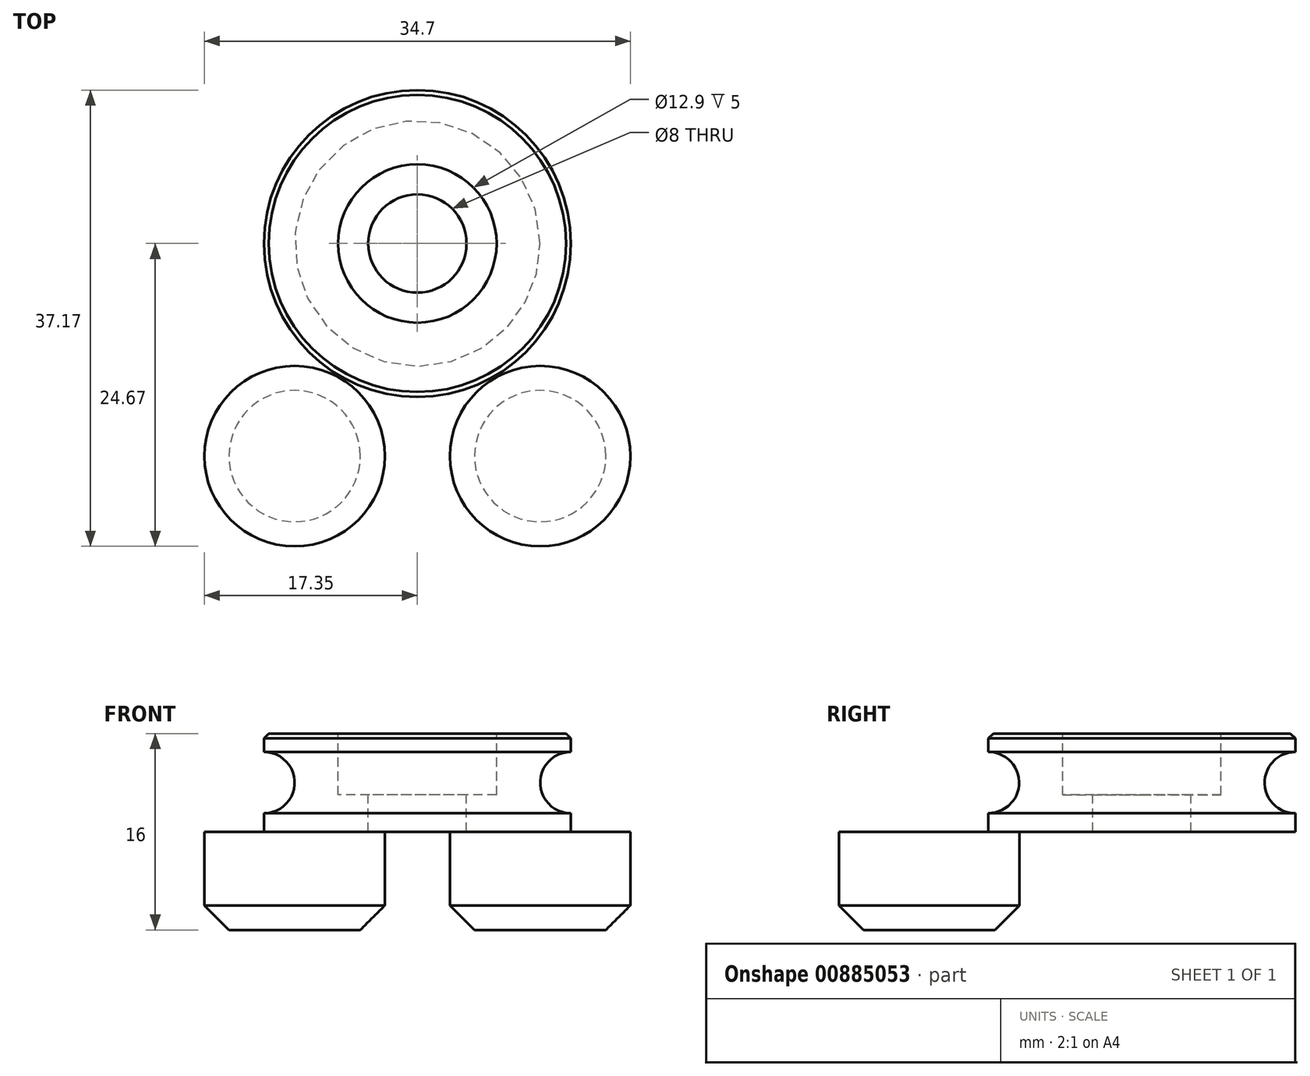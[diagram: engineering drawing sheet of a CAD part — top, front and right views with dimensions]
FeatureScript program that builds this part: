
annotation { "Feature Type Name" : "Feature", "Feature Type Description" : "" }
export const myFeature = defineFeature(function(context is Context, id is Id, definition is map)
    precondition{}
    {
        {
            var Q0;
            Q0=qCreatedBy(makeId("Top.planeOp"),FACE);
            var sketch = newSketch(context, id + "F0", { "sketchPlane" : qUnion([Q0])});
            skCircle(sketch, "E0", {"center": v(0, 0) * mm, "radius": 39 * mm});
            skCircle(sketch, "E1", {"center": v(0, 0) * mm, "radius": 2.33 * mm});
            skSolve(sketch);
        }
        {
            var Q0;
            Q0=qSketchRegion(id+"F0",true);
            extrude(context, id + "F1", {"entities" : qUnion([Q0]), "endBound" : BoundingType.SYMMETRIC, "depth" : 8 * mm, "offsetDistance" : 25 * mm});
        }
        {
            var Q0;
            Q0=qCreatedBy(makeId("Right.planeOp"),FACE);
            var sketch = newSketch(context, id + "F2", { "sketchPlane" : qUnion([Q0])});
            skLineSegment(sketch, "E2", {"start": v(43.5, 0) * mm, "end": v(-48.07, 0) * mm, "construction": true});
            skLineSegment(sketch, "E3", {"start": v(-39, -4) * mm, "end": v(-39, 4) * mm, "construction": true});
            skCircle(sketch, "E4", {"center": v(-39, 0) * mm, "radius": 2.5 * mm});
            skSolve(sketch);
        }
        {
            var Q0;
            Q0=qSketchRegion(id+"F2",true);
            var Q1;
            Q1=makeQuery(id+"F1.opExtrude","SWEPT_FACE",FACE,{"disambiguationData":[OSD([sQuery(id+"F0.wireOp",EDGE,"E1")])]});
            revolve(context, id + "F3", {"operationType" : NewBodyOperationType.REMOVE, "surfaceOperationType" : NewSurfaceOperationType.NEW, "entities" : qUnion([Q0]), "axis" : qUnion([Q1]), "revolveType" : RevolveType.FULL, "oppositeDirection" : true});
        }
        {
            var Q0;
            Q0=makeQuery(id+"F13.boolean.opBoolean","COPY",EDGE,{"derivedFrom":makeQuery(id+"F13.opExtrude","CAP_EDGE",EDGE,{"disambiguationData":[OSD([sQuery(id+"F12.wireOp",EDGE,"95e5c256-83ff-4b91-8d21-37ed4a70a4b7.2")])],"isStart":true})});
            var Q1;
            Q1=makeQuery(id+"F13.boolean.opBoolean","COPY",EDGE,{"derivedFrom":makeQuery(id+"F13.opExtrude","CAP_EDGE",EDGE,{"disambiguationData":[OSD([sQuery(id+"F12.wireOp",EDGE,"95e5c256-83ff-4b91-8d21-37ed4a70a4b7.3")])],"isStart":true})});
            var Q2;
            Q2=makeQuery(id+"F13.boolean.opBoolean","COPY",EDGE,{"derivedFrom":makeQuery(id+"F13.opExtrude","CAP_EDGE",EDGE,{"disambiguationData":[OSD([sQuery(id+"F12.wireOp",EDGE,"95e5c256-83ff-4b91-8d21-37ed4a70a4b7.4")])],"isStart":true})});
            var Q3;
            Q3=makeQuery(id+"F13.boolean.opBoolean","COPY",EDGE,{"derivedFrom":makeQuery(id+"F13.opExtrude","CAP_EDGE",EDGE,{"disambiguationData":[OSD([sQuery(id+"F12.wireOp",EDGE,"95e5c256-83ff-4b91-8d21-37ed4a70a4b7.5")])],"isStart":true})});
            var Q4;
            Q4=makeQuery(id+"F13.boolean.opBoolean","COPY",EDGE,{"derivedFrom":makeQuery(id+"F13.opExtrude","CAP_EDGE",EDGE,{"disambiguationData":[OSD([sQuery(id+"F12.wireOp",EDGE,"95e5c256-83ff-4b91-8d21-37ed4a70a4b7.0")])],"isStart":true})});
            var Q5;
            Q5=makeQuery(id+"F13.boolean.opBoolean","COPY",EDGE,{"derivedFrom":makeQuery(id+"F13.opExtrude","CAP_EDGE",EDGE,{"disambiguationData":[OSD([sQuery(id+"F12.wireOp",EDGE,"95e5c256-83ff-4b91-8d21-37ed4a70a4b7.1")])],"isStart":true})});
            var Q6;
            Q6=makeQuery(id+"F3.boolean.opBoolean","INTERSECT",EDGE,{"disambiguationData":[OD(1.0)],"derivedFrom":[makeQuery(id+"F1.opExtrude","SWEPT_FACE",FACE,{"disambiguationData":[OSD([sQuery(id+"F0.wireOp",EDGE,"E0")])]}),makeQuery(id+"F3.opRevolve","SWEPT_FACE",FACE,{"disambiguationData":[OSD([sQuery(id+"F2.wireOp",EDGE,"E4")])]})]});
            var Q7;
            Q7=makeQuery(id+"F3.boolean.opBoolean","INTERSECT",EDGE,{"disambiguationData":[OD(0.0)],"derivedFrom":[makeQuery(id+"F1.opExtrude","SWEPT_FACE",FACE,{"disambiguationData":[OSD([sQuery(id+"F0.wireOp",EDGE,"E0")])]}),makeQuery(id+"F3.opRevolve","SWEPT_FACE",FACE,{"disambiguationData":[OSD([sQuery(id+"F2.wireOp",EDGE,"E4")])]})]});
            chamfer(context, id + "F4", {"entities" : qUnion([Q0, Q1, Q2, Q3, Q4, Q5, Q6, Q7]), "width" : .5 * mm, "tangentPropagation" : true});
        }
        {
            var Q0;
            Q0=makeQuery(id+"F1.opExtrude","CAP_FACE",FACE,{"disambiguationData":[OSD([sQuery(id+"F0.wireOp",EDGE,"E0"),sQuery(id+"F0.wireOp",EDGE,"E1")])],"isStart":false});
            var sketch = newSketch(context, id + "F5", { "sketchPlane" : qUnion([Q0])});
            skCircle(sketch, "E5", {"center": v(-10, 17.32) * mm, "radius": 7.35 * mm});
            skLineSegment(sketch, "E6", {"start": v(0, -39) * mm, "end": v(0, 39) * mm, "construction": true});
            skLineSegment(sketch, "E7", {"start": v(39, 0) * mm, "end": v(-39, 0) * mm, "construction": true});
            skLineSegment(sketch, "E8", {"start": v(-2.6, -4.5) * mm, "end": v(19.5, 33.77) * mm, "construction": true});
            skLineSegment(sketch, "E9", {"start": v(2.6, -4.5) * mm, "end": v(-19.5, 33.77) * mm, "construction": true});
            skCircle(sketch, "E10", {"center": v(0, 0) * mm, "radius": 20 * mm, "construction": true});
            skCircle(sketch, "E11", {"center": v(-20, 0) * mm, "radius": 7.35 * mm});
            skCircle(sketch, "E12", {"center": v(10, 17.32) * mm, "radius": 7.35 * mm});
            skCircle(sketch, "E13", {"center": v(20, 0) * mm, "radius": 7.35 * mm});
            skCircle(sketch, "E14.MirrorC", {"center": v(10, -17.32) * mm, "radius": 7.35 * mm});
            skCircle(sketch, "E15.MirrorC", {"center": v(-10, -17.32) * mm, "radius": 7.35 * mm});
            skSolve(sketch);
        }
        {
            var Q0;
            Q0=makeQuery(id+"F5.imprint","IMPRINT",FACE,{"disambiguationData":[TD([[makeQuery(id+"F5.imprint","IMPRINT",EDGE,{"derivedFrom":sQuery(id+"F5.wireOp",EDGE,"E13")}),1.0]])]});
            var Q1;
            Q1=makeQuery(id+"F5.imprint","IMPRINT",FACE,{"disambiguationData":[TD([[makeQuery(id+"F5.imprint","IMPRINT",EDGE,{"derivedFrom":sQuery(id+"F5.wireOp",EDGE,"E14.MirrorC")}),-1.0]])]});
            var Q2;
            Q2=makeQuery(id+"F5.imprint","IMPRINT",FACE,{"disambiguationData":[TD([[makeQuery(id+"F5.imprint","IMPRINT",EDGE,{"derivedFrom":sQuery(id+"F5.wireOp",EDGE,"E15.MirrorC")}),-1.0]])]});
            var Q3;
            Q3=makeQuery(id+"F5.imprint","IMPRINT",FACE,{"disambiguationData":[TD([[makeQuery(id+"F5.imprint","IMPRINT",EDGE,{"derivedFrom":sQuery(id+"F5.wireOp",EDGE,"E11")}),1.0]])]});
            var Q4;
            Q4=makeQuery(id+"F5.imprint","IMPRINT",FACE,{"disambiguationData":[TD([[makeQuery(id+"F5.imprint","IMPRINT",EDGE,{"derivedFrom":sQuery(id+"F5.wireOp",EDGE,"E5")}),1.0]])]});
            var Q5;
            Q5=makeQuery(id+"F5.imprint","IMPRINT",FACE,{"disambiguationData":[TD([[makeQuery(id+"F5.imprint","IMPRINT",EDGE,{"derivedFrom":sQuery(id+"F5.wireOp",EDGE,"E12")}),1.0]])]});
            extrude(context, id + "F6", {"entities" : qUnion([Q0, Q1, Q2, Q3, Q4, Q5]), "operationType" : NewBodyOperationType.REMOVE, "oppositeDirection" : true, "depth" : 25 * mm, "offsetDistance" : 25 * mm});
        }
        {
            var Q0;
            Q0=makeQuery(id+"F6.boolean.opBoolean","INTERSECT",EDGE,{"derivedFrom":[makeQuery(id+"F1.opExtrude","CAP_FACE",FACE,{"disambiguationData":[OSD([sQuery(id+"F0.wireOp",EDGE,"E0"),sQuery(id+"F0.wireOp",EDGE,"E1")])],"isStart":true}),makeQuery(id+"F6.opExtrude","SWEPT_FACE",FACE,{"disambiguationData":[OSD([sQuery(id+"F5.wireOp",EDGE,"E11")])]})]});
            var Q1;
            Q1=makeQuery(id+"F6.boolean.opBoolean","INTERSECT",EDGE,{"derivedFrom":[makeQuery(id+"F1.opExtrude","CAP_FACE",FACE,{"disambiguationData":[OSD([sQuery(id+"F0.wireOp",EDGE,"E0"),sQuery(id+"F0.wireOp",EDGE,"E1")])],"isStart":true}),makeQuery(id+"F6.opExtrude","SWEPT_FACE",FACE,{"disambiguationData":[OSD([sQuery(id+"F5.wireOp",EDGE,"E15.MirrorC")])]})]});
            var Q2;
            Q2=makeQuery(id+"F6.boolean.opBoolean","INTERSECT",EDGE,{"derivedFrom":[makeQuery(id+"F1.opExtrude","CAP_FACE",FACE,{"disambiguationData":[OSD([sQuery(id+"F0.wireOp",EDGE,"E0"),sQuery(id+"F0.wireOp",EDGE,"E1")])],"isStart":true}),makeQuery(id+"F6.opExtrude","SWEPT_FACE",FACE,{"disambiguationData":[OSD([sQuery(id+"F5.wireOp",EDGE,"E14.MirrorC")])]})]});
            var Q3;
            Q3=makeQuery(id+"F6.boolean.opBoolean","INTERSECT",EDGE,{"derivedFrom":[makeQuery(id+"F1.opExtrude","CAP_FACE",FACE,{"disambiguationData":[OSD([sQuery(id+"F0.wireOp",EDGE,"E0"),sQuery(id+"F0.wireOp",EDGE,"E1")])],"isStart":true}),makeQuery(id+"F6.opExtrude","SWEPT_FACE",FACE,{"disambiguationData":[OSD([sQuery(id+"F5.wireOp",EDGE,"E13")])]})]});
            var Q4;
            Q4=makeQuery(id+"F6.boolean.opBoolean","INTERSECT",EDGE,{"derivedFrom":[makeQuery(id+"F1.opExtrude","CAP_FACE",FACE,{"disambiguationData":[OSD([sQuery(id+"F0.wireOp",EDGE,"E0"),sQuery(id+"F0.wireOp",EDGE,"E1")])],"isStart":true}),makeQuery(id+"F6.opExtrude","SWEPT_FACE",FACE,{"disambiguationData":[OSD([sQuery(id+"F5.wireOp",EDGE,"E12")])]})]});
            var Q5;
            Q5=makeQuery(id+"F6.boolean.opBoolean","INTERSECT",EDGE,{"derivedFrom":[makeQuery(id+"F1.opExtrude","CAP_FACE",FACE,{"disambiguationData":[OSD([sQuery(id+"F0.wireOp",EDGE,"E0"),sQuery(id+"F0.wireOp",EDGE,"E1")])],"isStart":true}),makeQuery(id+"F6.opExtrude","SWEPT_FACE",FACE,{"disambiguationData":[OSD([sQuery(id+"F5.wireOp",EDGE,"E5")])]})]});
            chamfer(context, id + "F7", {"entities" : qUnion([Q0, Q1, Q2, Q3, Q4, Q5]), "width" : 2 * mm, "tangentPropagation" : true});
        }
        {
            var Q0;
            Q0=makeQuery(id+"F1.opExtrude","CAP_FACE",FACE,{"disambiguationData":[OSD([sQuery(id+"F0.wireOp",EDGE,"E0"),sQuery(id+"F0.wireOp",EDGE,"E1")])],"isStart":false});
            var sketch = newSketch(context, id + "F8", { "sketchPlane" : qUnion([Q0])});
            skCircle(sketch, "E16", {"center": v(0, 0) * mm, "radius": 12.5 * mm});
            skSolve(sketch);
        }
        {
            var Q0;
            Q0 = qSketchRegion(id + "F8", true);
            extrude(context, id + "F9", {"entities" : qUnion([Q0]), "operationType" : NewBodyOperationType.ADD, "depth" : 8 * mm, "offsetDistance" : 25 * mm});
        }
        {
            var Q0;
            Q0=qCreatedBy(makeId("Right.planeOp"),FACE);
            var sketch = newSketch(context, id + "F10", { "sketchPlane" : qUnion([Q0])});
            skLineSegment(sketch, "E17", {"start": v(12.5, 10.5) * mm, "end": v(12.5, 5.5) * mm});
            skLineSegment(sketch, "E18", {"start": v(12.5, 8) * mm, "end": v(0, 8) * mm, "construction": true});
            skArc(sketch, "E19", {"start": v(12.5, 10.5) * mm, "mid": v(10, 8) * mm, "end": v(12.5, 5.5) * mm});
            skPoint(sketch, "E20.0.end.orphan", {"position": v(12.5, 12) * mm});
            skPoint(sketch, "E20.0.start.orphan", {"position": v(-12.5, 12) * mm});
            skPoint(sketch, "E21.0.end.orphan", {"position": v(12.5, 4) * mm});
            skPoint(sketch, "E21.0.start.orphan", {"position": v(12.32, 4) * mm});
            skSolve(sketch);
        }
        {
            var Q0;
            Q0 = qSketchRegion(id + "F10", true);
            var Q1;
            Q1=makeQuery(id+"F9.opExtrude","SWEPT_FACE",FACE,{"disambiguationData":[OSD([sQuery(id+"F8.wireOp",EDGE,"E16")])]});
            revolve(context, id + "F11", {"operationType" : NewBodyOperationType.REMOVE, "surfaceOperationType" : NewSurfaceOperationType.NEW, "entities" : qUnion([Q0]), "axis" : qUnion([Q1]), "revolveType" : RevolveType.FULL});
        }
        {
            var Q0;
            Q0=makeQuery(id+"F9.opExtrude","CAP_FACE",FACE,{"disambiguationData":[OSD([sQuery(id+"F8.wireOp",EDGE,"E16")])],"isStart":false});
            var sketch = newSketch(context, id + "F12", { "sketchPlane" : qUnion([Q0])});
            skCircle(sketch, "E22", {"center": v(0, 0) * mm, "radius": 6.45 * mm});
            skSolve(sketch);
        }
        {
            var Q0;
            Q0=makeQuery(id+"F12.imprint","IMPRINT",FACE,{"disambiguationData":[TD([[makeQuery(id+"F12.imprint","IMPRINT",EDGE,{"derivedFrom":sQuery(id+"F12.wireOp",EDGE,"E22")}),1.0]])]});
            extrude(context, id + "F13", {"entities" : qUnion([Q0]), "operationType" : NewBodyOperationType.REMOVE, "oppositeDirection" : true, "depth" : 5 * mm, "offsetDistance" : 25 * mm});
        }
        {
            var Q0;
            Q0=makeQuery(id+"F1.opExtrude","CAP_FACE",FACE,{"disambiguationData":[OSD([sQuery(id+"F0.wireOp",EDGE,"E0"),sQuery(id+"F0.wireOp",EDGE,"E1")])],"isStart":true});
            var sketch = newSketch(context, id + "F14", { "sketchPlane" : qUnion([Q0])});
            skCircle(sketch, "E23", {"center": v(0, 0) * mm, "radius": 6.45 * mm});
            skSolve(sketch);
        }
        {
            var Q0;
            Q0 = qSketchRegion(id + "F14", true);
            extrude(context, id + "F15", {"entities" : qUnion([Q0]), "operationType" : NewBodyOperationType.REMOVE, "oppositeDirection" : true, "depth" : 5 * mm, "offsetDistance" : 25 * mm});
        }
        {
            var Q0;
            Q0=makeQuery(id+"F9.opExtrude","CAP_EDGE",EDGE,{"disambiguationData":[OSD([sQuery(id+"F8.wireOp",EDGE,"E16")])],"isStart":false});
            var Q1;
            Q1=makeQuery(id+"F13.boolean.opBoolean","COPY",EDGE,{"derivedFrom":makeQuery(id+"F13.opExtrude","CAP_EDGE",EDGE,{"disambiguationData":[OSD([sQuery(id+"F12.wireOp",EDGE,"95e5c256-83ff-4b91-8d21-37ed4a70a4b7.0")])],"isStart":true})});
            var Q2;
            Q2=makeQuery(id+"F13.boolean.opBoolean","COPY",EDGE,{"derivedFrom":makeQuery(id+"F13.opExtrude","CAP_EDGE",EDGE,{"disambiguationData":[OSD([sQuery(id+"F12.wireOp",EDGE,"95e5c256-83ff-4b91-8d21-37ed4a70a4b7.1")])],"isStart":true})});
            var Q3;
            Q3=makeQuery(id+"F13.boolean.opBoolean","COPY",EDGE,{"derivedFrom":makeQuery(id+"F13.opExtrude","CAP_EDGE",EDGE,{"disambiguationData":[OSD([sQuery(id+"F12.wireOp",EDGE,"95e5c256-83ff-4b91-8d21-37ed4a70a4b7.2")])],"isStart":true})});
            var Q4;
            Q4=makeQuery(id+"F13.boolean.opBoolean","COPY",EDGE,{"derivedFrom":makeQuery(id+"F13.opExtrude","CAP_EDGE",EDGE,{"disambiguationData":[OSD([sQuery(id+"F12.wireOp",EDGE,"95e5c256-83ff-4b91-8d21-37ed4a70a4b7.3")])],"isStart":true})});
            var Q5;
            Q5=makeQuery(id+"F13.boolean.opBoolean","COPY",EDGE,{"derivedFrom":makeQuery(id+"F13.opExtrude","CAP_EDGE",EDGE,{"disambiguationData":[OSD([sQuery(id+"F12.wireOp",EDGE,"95e5c256-83ff-4b91-8d21-37ed4a70a4b7.4")])],"isStart":true})});
            var Q6;
            Q6=makeQuery(id+"F13.boolean.opBoolean","COPY",EDGE,{"derivedFrom":makeQuery(id+"F13.opExtrude","CAP_EDGE",EDGE,{"disambiguationData":[OSD([sQuery(id+"F12.wireOp",EDGE,"95e5c256-83ff-4b91-8d21-37ed4a70a4b7.5")])],"isStart":true})});
            var Q7;
            Q7=makeQuery(id+"F13.boolean.opBoolean","COPY",EDGE,{"derivedFrom":makeQuery(id+"F13.opExtrude","CAP_EDGE",EDGE,{"disambiguationData":[OSD([sQuery(id+"F12.wireOp",EDGE,"E22")])],"isStart":true})});
            var Q8;
            Q8=makeQuery(id+"F15.boolean.opBoolean","COPY",EDGE,{"derivedFrom":makeQuery(id+"F15.opExtrude","CAP_EDGE",EDGE,{"disambiguationData":[OSD([sQuery(id+"F14.wireOp",EDGE,"E23")])],"isStart":true})});
            chamfer(context, id + "F16", {"entities" : qUnion([Q0, Q1, Q2, Q3, Q4, Q5, Q6, Q7, Q8]), "width" : .4 * mm, "tangentPropagation" : true});
        }
        {
            var Q0;
            Q0=makeQuery(id+"F13.boolean.opBoolean","COPY",FACE,{"derivedFrom":makeQuery(id+"F13.opExtrude","CAP_FACE",FACE,{"disambiguationData":[OSD([sQuery(id+"F12.wireOp",EDGE,"E22")])],"isStart":false})});
            var sketch = newSketch(context, id + "F17", { "sketchPlane" : qUnion([Q0])});
            skCircle(sketch, "E24", {"center": v(0, 0) * mm, "radius": 4 * mm});
            skSolve(sketch);
        }
        {
            var Q0;
            Q0 = qSketchRegion(id + "F17", true);
            extrude(context, id + "F18", {"entities" : qUnion([Q0]), "operationType" : NewBodyOperationType.REMOVE, "endBound" : BoundingType.THROUGH_ALL, "oppositeDirection" : true, "depth" : 25 * mm, "offsetDistance" : 25 * mm});
        }
    });
